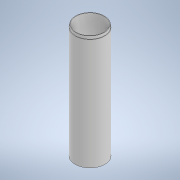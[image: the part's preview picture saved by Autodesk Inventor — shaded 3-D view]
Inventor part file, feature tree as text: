
AUTODESK INVENTOR PART (.ipt)
format: ipt  version: 2020.3 (Build 243373000, 373)  size: 106,496 bytes
history: native  units: mm
features: extrude x2, sketch x1
ambient origin geometry x8: Origin, YZ Plane, XZ Plane, XY Plane, X Axis, Y Axis, Z Axis, Center Point
bodies: Solid1 (feature_tree)
feature tree (3):
  sketch  "Sketch1"  dims[d0=51.8mm d1=50.0mm d2=53.6mm d3=200.0mm d4=0.0mm d5=95.0mm d6=105.0mm d7=0.0mm d8=0.0mm]
  extrude  "Extrusion1"  Depth=95.0mm TaperAngle=0.0deg
  extrude  "Extrusion2"  [1 undecoded]
note: 1 required parameter value undecoded (feature->parameter linkage not recoverable at this tier; creation-order binding heuristic only, values carry confidence <= 0.55)
